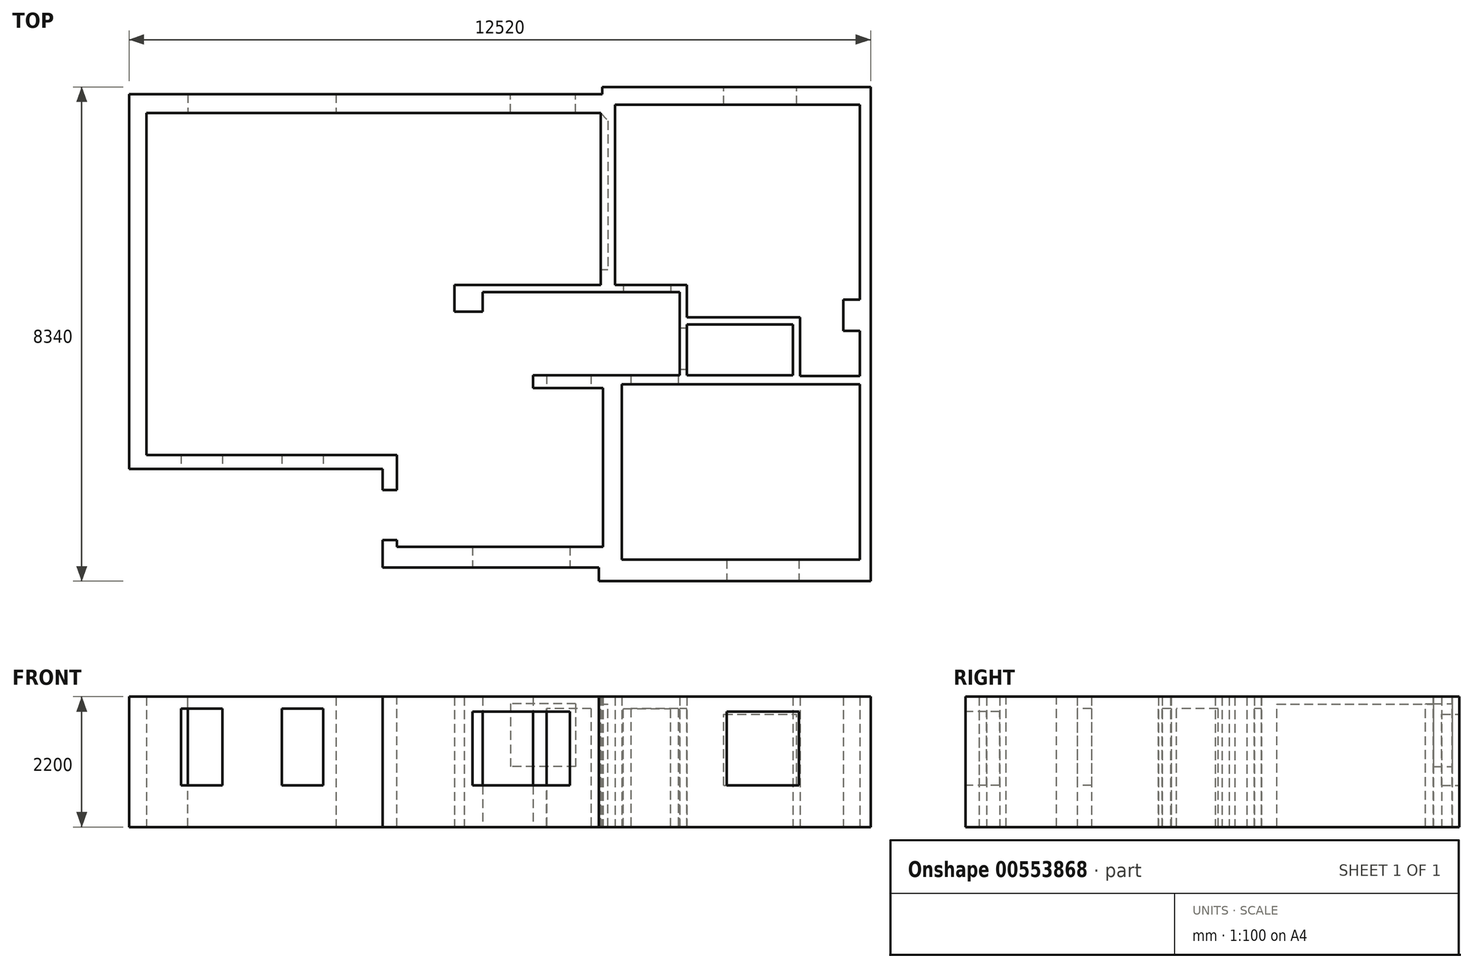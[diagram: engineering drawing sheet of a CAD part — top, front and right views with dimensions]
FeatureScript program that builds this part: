
annotation { "Feature Type Name" : "Feature", "Feature Type Description" : "" }
export const myFeature = defineFeature(function(context is Context, id is Id, definition is map)
    precondition{}
    {
        {
            var Q0;
            Q0=qCreatedBy(makeId("Top.planeOp"),FACE);
            var sketch = newSketch(context, id + "F0", { "sketchPlane" : qUnion([Q0])});
            skLineSegment(sketch, "E0", {"start": v(890, -1585.96) * mm, "end": v(-3390, -1585.96) * mm});
            skLineSegment(sketch, "E1", {"start": v(-3390, 4744.04) * mm, "end": v(-3390, -1585.96) * mm});
            skLineSegment(sketch, "E2", {"start": v(890, -3245.96) * mm, "end": v(4540, -3245.96) * mm});
            skLineSegment(sketch, "E3", {"start": v(4610, -2895.96) * mm, "end": v(1130, -2895.96) * mm});
            skLineSegment(sketch, "E4", {"start": v(4540, -3245.96) * mm, "end": v(4540, -3475.96) * mm});
            skLineSegment(sketch, "E5", {"start": v(4540, -3475.96) * mm, "end": v(9130, -3475.96) * mm});
            skLineSegment(sketch, "E6", {"start": v(9130, -3475.96) * mm, "end": v(9130, 4864.04) * mm});
            skLineSegment(sketch, "E7", {"start": v(9130, 4864.04) * mm, "end": v(4600, 4864.04) * mm});
            skLineSegment(sketch, "E8", {"start": v(4815, 4564.04) * mm, "end": v(8950, 4564.04) * mm});
            skLineSegment(sketch, "E9", {"start": v(8950, -3115.96) * mm, "end": v(4930, -3115.96) * mm});
            skLineSegment(sketch, "E10", {"start": v(8950, -155.96) * mm, "end": v(4930, -155.96) * mm});
            skLineSegment(sketch, "E11.bottom", {"start": v(8950, 1274.04) * mm, "end": v(8670, 1274.04) * mm});
            skLineSegment(sketch, "E11.top", {"start": v(8950, 744.04) * mm, "end": v(8670, 744.04) * mm});
            skLineSegment(sketch, "E11.right", {"start": v(8670, 1274.04) * mm, "end": v(8670, 744.04) * mm});
            skLineSegment(sketch, "E12", {"start": v(2020, 4424.04) * mm, "end": v(2020, 1518.96) * mm});
            skLineSegment(sketch, "E13", {"start": v(2020, 1518.96) * mm, "end": v(1110, 1518.96) * mm});
            skLineSegment(sketch, "E14", {"start": v(5905, 1400) * mm, "end": v(5905, 0) * mm});
            skLineSegment(sketch, "E15", {"start": v(7935, -15.96) * mm, "end": v(7935, 974.04) * mm});
            skLineSegment(sketch, "E16", {"start": v(7935, 974.04) * mm, "end": v(6025, 974.04) * mm});
            skLineSegment(sketch, "E17", {"start": v(6025, 974.04) * mm, "end": v(6025, 1524.04) * mm});
            skLineSegment(sketch, "E18", {"start": v(6025, 1524.04) * mm, "end": v(4815, 1524.04) * mm});
            skLineSegment(sketch, "E19", {"start": v(4815, 1524.04) * mm, "end": v(4815, 4564.04) * mm});
            skLineSegment(sketch, "E20", {"start": v(4695, 1524.04) * mm, "end": v(2215, 1524.04) * mm});
            skLineSegment(sketch, "E21", {"start": v(2215, 1524.04) * mm, "end": v(2215, 4424.04) * mm});
            skLineSegment(sketch, "E22", {"start": v(2100, 1400) * mm, "end": v(2100, 1070) * mm});
            skLineSegment(sketch, "E23", {"start": v(2100, 1070) * mm, "end": v(2580, 1070) * mm});
            skLineSegment(sketch, "E24", {"start": v(2580, 1070) * mm, "end": v(2580, 1400) * mm});
            skLineSegment(sketch, "E25", {"start": v(4695, 4424.04) * mm, "end": v(4695, 1524.04) * mm});
            skLineSegment(sketch, "E26", {"start": v(4695, 4424.04) * mm, "end": v(2215, 4424.04) * mm});
            skLineSegment(sketch, "E27", {"start": v(2020, 4424.04) * mm, "end": v(-3100, 4424.04) * mm});
            skLineSegment(sketch, "E28", {"start": v(-3100, 4424.04) * mm, "end": v(-3100, -1345.96) * mm});
            skLineSegment(sketch, "E29", {"start": v(890, -1585.96) * mm, "end": v(890, -3245.96) * mm});
            skLineSegment(sketch, "E30", {"start": v(4610, -215.96) * mm, "end": v(4610, -2895.96) * mm});
            skLineSegment(sketch, "E31", {"start": v(4930, -155.96) * mm, "end": v(4930, -3115.96) * mm});
            skLineSegment(sketch, "E32", {"start": v(8950, -155.96) * mm, "end": v(8950, -3115.96) * mm});
            skLineSegment(sketch, "E33", {"start": v(8950, -15.96) * mm, "end": v(8950, 744.04) * mm});
            skLineSegment(sketch, "E34", {"start": v(8950, 1274.04) * mm, "end": v(8950, 4564.04) * mm});
            skLineSegment(sketch, "E35", {"start": v(7935, -15.96) * mm, "end": v(8950, -15.96) * mm});
            skLineSegment(sketch, "E36", {"start": v(1110, 1400) * mm, "end": v(2100, 1400) * mm});
            skLineSegment(sketch, "E37", {"start": v(2580, 1400) * mm, "end": v(5905, 1400) * mm});
            skLineSegment(sketch, "E38", {"start": v(4610, -215.96) * mm, "end": v(3430, -215.96) * mm});
            skLineSegment(sketch, "E39", {"start": v(1130, -1345.96) * mm, "end": v(1130, -2895.96) * mm});
            skLineSegment(sketch, "E40", {"start": v(4600, 4864.04) * mm, "end": v(4600, 4744.04) * mm});
            skLineSegment(sketch, "E41", {"start": v(4600, 4744.04) * mm, "end": v(-3390, 4744.04) * mm});
            skLineSegment(sketch, "E42", {"start": v(-3100, -1345.96) * mm, "end": v(1130, -1345.96) * mm});
            skLineSegment(sketch, "E43", {"start": v(1110, 1400) * mm, "end": v(1110, 1518.96) * mm});
            skLineSegment(sketch, "E44", {"start": v(3430, -215.96) * mm, "end": v(3430, 0) * mm});
            skLineSegment(sketch, "E45", {"start": v(3430, 0) * mm, "end": v(5905, 0) * mm});
            skLineSegment(sketch, "E46.bottom", {"start": v(7815, 854.04) * mm, "end": v(6025, 854.04) * mm});
            skLineSegment(sketch, "E46.top", {"start": v(7815, 0) * mm, "end": v(6025, 0) * mm});
            skLineSegment(sketch, "E46.left", {"start": v(7815, 854.04) * mm, "end": v(7815, 0) * mm});
            skLineSegment(sketch, "E46.right", {"start": v(6025, 854.04) * mm, "end": v(6025, 0) * mm});
            skSolve(sketch);
        }
        {
            var Q0;
            Q0=makeQuery(id+"F0.imprint","IMPRINT",FACE,{"disambiguationData":[TD([[makeQuery(id+"F0.imprint","IMPRINT",EDGE,{"derivedFrom":sQuery(id+"F0.wireOp",EDGE,"E0")}),-1.0]])]});
            extrude(context, id + "F1", {"entities" : qUnion([Q0]), "depth" : 2200 * mm});
        }
        {
            var Q0;
            Q0=makeQuery(id+"F1.opExtrude","SWEPT_FACE",FACE,{"disambiguationData":[OSD([sQuery(id+"F0.wireOp",EDGE,"E27")])]});
            var sketch = newSketch(context, id + "F2", { "sketchPlane" : qUnion([Q0])});
            skLineSegment(sketch, "E47", {"start": v(-2400, 0) * mm, "end": v(-2400, 2199) * mm});
            skLineSegment(sketch, "E48", {"start": v(-2400, 2199) * mm, "end": v(100, 2199) * mm});
            skLineSegment(sketch, "E49", {"start": v(100, 2199) * mm, "end": v(100, 0) * mm});
            skLineSegment(sketch, "E50", {"start": v(100, 0) * mm, "end": v(-2400, 0) * mm});
            skSolve(sketch);
        }
        {
            var Q0;
            Q0=qSketchRegion(id+"F2",true);
            extrude(context, id + "F3", {"entities" : qUnion([Q0]), "operationType" : NewBodyOperationType.REMOVE, "oppositeDirection" : true, "depth" : 350 * mm});
        }
        {
            var Q0;
            Q0=makeQuery(id+"F1.opExtrude","SWEPT_FACE",FACE,{"disambiguationData":[OSD([sQuery(id+"F0.wireOp",EDGE,"E12")])]});
            var sketch = newSketch(context, id + "F4", { "sketchPlane" : qUnion([Q0])});
            skLineSegment(sketch, "E51", {"start": v(-4424.04, 0) * mm, "end": v(-4424.04, 2200) * mm});
            skLineSegment(sketch, "E52", {"start": v(-4424.04, 2200) * mm, "end": v(-1518.96, 2200) * mm});
            skLineSegment(sketch, "E53", {"start": v(-1518.96, 2200) * mm, "end": v(-1518.96, 0) * mm});
            skLineSegment(sketch, "E54", {"start": v(-1518.96, 0) * mm, "end": v(-4424.04, 0) * mm});
            skSolve(sketch);
        }
        {
            var Q0;
            Q0=qSketchRegion(id+"F4",true);
            extrude(context, id + "F5", {"entities" : qUnion([Q0]), "operationType" : NewBodyOperationType.REMOVE, "oppositeDirection" : true, "depth" : 250 * mm});
        }
        {
            var Q0;
            Q0=makeQuery(id+"F1.opExtrude","SWEPT_FACE",FACE,{"disambiguationData":[OSD([sQuery(id+"F0.wireOp",EDGE,"E36")])]});
            var sketch = newSketch(context, id + "F6", { "sketchPlane" : qUnion([Q0])});
            skLineSegment(sketch, "E55.bottom", {"start": v(1110, 0) * mm, "end": v(2100, 0) * mm});
            skLineSegment(sketch, "E55.top", {"start": v(1110, 2200) * mm, "end": v(2100, 2200) * mm});
            skLineSegment(sketch, "E55.left", {"start": v(1110, 0) * mm, "end": v(1110, 2200) * mm});
            skLineSegment(sketch, "E55.right", {"start": v(2100, 0) * mm, "end": v(2100, 2200) * mm});
            skSolve(sketch);
        }
        {
            var Q0;
            Q0=qSketchRegion(id+"F6",true);
            extrude(context, id + "F7", {"entities" : qUnion([Q0]), "operationType" : NewBodyOperationType.REMOVE, "oppositeDirection" : true, "depth" : 130 * mm});
        }
        {
            var Q0;
            Q0=makeQuery(id+"F1.opExtrude","SWEPT_FACE",FACE,{"disambiguationData":[OSD([sQuery(id+"F0.wireOp",EDGE,"E38")])]});
            var sketch = newSketch(context, id + "F8", { "sketchPlane" : qUnion([Q0])});
            skLineSegment(sketch, "E56.bottom", {"start": v(3660, 0) * mm, "end": v(4410, 0) * mm});
            skLineSegment(sketch, "E56.top", {"start": v(3660, 2000) * mm, "end": v(4410, 2000) * mm});
            skLineSegment(sketch, "E56.left", {"start": v(3660, 0) * mm, "end": v(3660, 2000) * mm});
            skLineSegment(sketch, "E56.right", {"start": v(4410, 0) * mm, "end": v(4410, 2000) * mm});
            skSolve(sketch);
        }
        {
            var Q0;
            Q0=qSketchRegion(id+"F8",true);
            extrude(context, id + "F9", {"entities" : qUnion([Q0]), "operationType" : NewBodyOperationType.REMOVE, "oppositeDirection" : true, "depth" : 250 * mm});
        }
        {
            var Q0;
            Q0=makeQuery(id+"F1.opExtrude","SWEPT_FACE",FACE,{"disambiguationData":[OSD([sQuery(id+"F0.wireOp",EDGE,"E37")])]});
            var sketch = newSketch(context, id + "F10", { "sketchPlane" : qUnion([Q0])});
            skLineSegment(sketch, "E57.bottom", {"start": v(4955, 0) * mm, "end": v(5755, 0) * mm});
            skLineSegment(sketch, "E57.top", {"start": v(4955, 2000) * mm, "end": v(5755, 2000) * mm});
            skLineSegment(sketch, "E57.left", {"start": v(4955, 0) * mm, "end": v(4955, 2000) * mm});
            skLineSegment(sketch, "E57.right", {"start": v(5755, 0) * mm, "end": v(5755, 2000) * mm});
            skSolve(sketch);
        }
        {
            var Q0;
            Q0=qSketchRegion(id+"F10",true);
            extrude(context, id + "F11", {"entities" : qUnion([Q0]), "operationType" : NewBodyOperationType.REMOVE, "oppositeDirection" : true, "depth" : 200 * mm});
        }
        {
            var Q0;
            Q0=makeQuery(id+"F1.opExtrude","SWEPT_FACE",FACE,{"disambiguationData":[OSD([sQuery(id+"F0.wireOp",EDGE,"E10")])]});
            var sketch = newSketch(context, id + "F12", { "sketchPlane" : qUnion([Q0])});
            skLineSegment(sketch, "E58.bottom", {"start": v(5080, 0) * mm, "end": v(5880, 0) * mm});
            skLineSegment(sketch, "E58.top", {"start": v(5080, 2000) * mm, "end": v(5880, 2000) * mm});
            skLineSegment(sketch, "E58.left", {"start": v(5080, 0) * mm, "end": v(5080, 2000) * mm});
            skLineSegment(sketch, "E58.right", {"start": v(5880, 0) * mm, "end": v(5880, 2000) * mm});
            skSolve(sketch);
        }
        {
            var Q0;
            Q0=qSketchRegion(id+"F12",true);
            extrude(context, id + "F13", {"entities" : qUnion([Q0]), "operationType" : NewBodyOperationType.REMOVE, "oppositeDirection" : true, "depth" : 200 * mm});
        }
        {
            var Q0;
            Q0=makeQuery(id+"F1.opExtrude","SWEPT_FACE",FACE,{"disambiguationData":[OSD([sQuery(id+"F0.wireOp",EDGE,"E0")])]});
            var sketch = newSketch(context, id + "F14", { "sketchPlane" : qUnion([Q0])});
            skLineSegment(sketch, "E59.bottom", {"start": v(-2515, 2000) * mm, "end": v(-1815, 2000) * mm});
            skLineSegment(sketch, "E59.top", {"start": v(-2515, 700) * mm, "end": v(-1815, 700) * mm});
            skLineSegment(sketch, "E59.left", {"start": v(-2515, 2000) * mm, "end": v(-2515, 700) * mm});
            skLineSegment(sketch, "E59.right", {"start": v(-1815, 2000) * mm, "end": v(-1815, 700) * mm});
            skLineSegment(sketch, "E60.bottom", {"start": v(-815, 2000) * mm, "end": v(-115, 2000) * mm});
            skLineSegment(sketch, "E60.top", {"start": v(-815, 700) * mm, "end": v(-115, 700) * mm});
            skLineSegment(sketch, "E60.left", {"start": v(-815, 2000) * mm, "end": v(-815, 700) * mm});
            skLineSegment(sketch, "E60.right", {"start": v(-115, 2000) * mm, "end": v(-115, 700) * mm});
            skSolve(sketch);
        }
        {
            var Q0;
            Q0=qSketchRegion(id+"F14",true);
            extrude(context, id + "F15", {"entities" : qUnion([Q0]), "operationType" : NewBodyOperationType.REMOVE, "endBound" : BoundingType.UP_TO_NEXT, "oppositeDirection" : true, "depth" : 350 * mm});
        }
        {
            var Q0;
            Q0=makeQuery(id+"F1.opExtrude","SWEPT_FACE",FACE,{"disambiguationData":[OSD([sQuery(id+"F0.wireOp",EDGE,"E2")])]});
            var sketch = newSketch(context, id + "F16", { "sketchPlane" : qUnion([Q0])});
            skLineSegment(sketch, "E61.bottom", {"start": v(2410, 1950) * mm, "end": v(4050, 1950) * mm});
            skLineSegment(sketch, "E61.top", {"start": v(2410, 700) * mm, "end": v(4050, 700) * mm});
            skLineSegment(sketch, "E61.left", {"start": v(2410, 1950) * mm, "end": v(2410, 700) * mm});
            skLineSegment(sketch, "E61.right", {"start": v(4050, 1950) * mm, "end": v(4050, 700) * mm});
            skSolve(sketch);
        }
        {
            var Q0;
            Q0=qSketchRegion(id+"F16",true);
            extrude(context, id + "F17", {"entities" : qUnion([Q0]), "operationType" : NewBodyOperationType.REMOVE, "endBound" : BoundingType.UP_TO_NEXT, "oppositeDirection" : true, "depth" : 25 * mm});
        }
        {
            var Q0;
            Q0=makeQuery(id+"F1.opExtrude","SWEPT_FACE",FACE,{"disambiguationData":[OSD([sQuery(id+"F0.wireOp",EDGE,"E5")])]});
            var sketch = newSketch(context, id + "F18", { "sketchPlane" : qUnion([Q0])});
            skLineSegment(sketch, "E62.bottom", {"start": v(6700, 1950) * mm, "end": v(7920, 1950) * mm});
            skLineSegment(sketch, "E62.top", {"start": v(6700, 700) * mm, "end": v(7920, 700) * mm});
            skLineSegment(sketch, "E62.left", {"start": v(6700, 1950) * mm, "end": v(6700, 700) * mm});
            skLineSegment(sketch, "E62.right", {"start": v(7920, 1950) * mm, "end": v(7920, 700) * mm});
            skSolve(sketch);
        }
        {
            var Q0;
            Q0=qSketchRegion(id+"F18",true);
            extrude(context, id + "F19", {"entities" : qUnion([Q0]), "operationType" : NewBodyOperationType.REMOVE, "endBound" : BoundingType.UP_TO_NEXT, "oppositeDirection" : true, "depth" : 25 * mm});
        }
        {
            var Q0;
            Q0=makeQuery(id+"F1.opExtrude","SWEPT_FACE",FACE,{"disambiguationData":[OSD([sQuery(id+"F0.wireOp",EDGE,"E7")])]});
            var sketch = newSketch(context, id + "F20", { "sketchPlane" : qUnion([Q0])});
            skLineSegment(sketch, "E63.bottom", {"start": v(-7880, 1900) * mm, "end": v(-6650, 1900) * mm});
            skLineSegment(sketch, "E63.top", {"start": v(-7880, 700) * mm, "end": v(-6650, 700) * mm});
            skLineSegment(sketch, "E63.left", {"start": v(-7880, 1900) * mm, "end": v(-7880, 700) * mm});
            skLineSegment(sketch, "E63.right", {"start": v(-6650, 1900) * mm, "end": v(-6650, 700) * mm});
            skSolve(sketch);
        }
        {
            var Q0;
            Q0=qSketchRegion(id+"F20",true);
            extrude(context, id + "F21", {"entities" : qUnion([Q0]), "operationType" : NewBodyOperationType.REMOVE, "endBound" : BoundingType.UP_TO_NEXT, "oppositeDirection" : true, "depth" : 25 * mm});
        }
        {
            var Q0;
            Q0=makeQuery(id+"F1.opExtrude","SWEPT_FACE",FACE,{"disambiguationData":[OSD([sQuery(id+"F0.wireOp",EDGE,"E41")])]});
            var sketch = newSketch(context, id + "F22", { "sketchPlane" : qUnion([Q0])});
            skLineSegment(sketch, "E64.bottom", {"start": v(-4150, 2080) * mm, "end": v(-3050, 2080) * mm});
            skLineSegment(sketch, "E64.top", {"start": v(-4150, 1020) * mm, "end": v(-3050, 1020) * mm});
            skLineSegment(sketch, "E64.left", {"start": v(-4150, 2080) * mm, "end": v(-4150, 1020) * mm});
            skLineSegment(sketch, "E64.right", {"start": v(-3050, 2080) * mm, "end": v(-3050, 1020) * mm});
            skSolve(sketch);
        }
        {
            var Q0;
            Q0=qSketchRegion(id+"F22",true);
            extrude(context, id + "F23", {"entities" : qUnion([Q0]), "operationType" : NewBodyOperationType.REMOVE, "endBound" : BoundingType.UP_TO_NEXT, "oppositeDirection" : true, "depth" : 25 * mm});
        }
        {
            var Q0;
            Q0=makeQuery(id+"F1.opExtrude","SWEPT_FACE",FACE,{"disambiguationData":[OSD([sQuery(id+"F0.wireOp",EDGE,"E29")])]});
            var sketch = newSketch(context, id + "F24", { "sketchPlane" : qUnion([Q0])});
            skLineSegment(sketch, "E65.bottom", {"start": v(1935.96, 0) * mm, "end": v(2785.96, 0) * mm});
            skLineSegment(sketch, "E65.top", {"start": v(1935.96, 2200) * mm, "end": v(2785.96, 2200) * mm});
            skLineSegment(sketch, "E65.left", {"start": v(1935.96, 0) * mm, "end": v(1935.96, 2200) * mm});
            skLineSegment(sketch, "E65.right", {"start": v(2785.96, 0) * mm, "end": v(2785.96, 2200) * mm});
            skSolve(sketch);
        }
        {
            var Q0;
            Q0=qSketchRegion(id+"F24",true);
            extrude(context, id + "F25", {"entities" : qUnion([Q0]), "operationType" : NewBodyOperationType.REMOVE, "endBound" : BoundingType.UP_TO_NEXT, "oppositeDirection" : true, "depth" : 25 * mm});
        }
        {
            var Q0;
            Q0=makeQuery(id+"F1.opExtrude","SWEPT_FACE",FACE,{"disambiguationData":[OSD([sQuery(id+"F0.wireOp",EDGE,"E14")])]});
            var sketch = newSketch(context, id + "F26", { "sketchPlane" : qUnion([Q0])});
            skLineSegment(sketch, "E66.bottom", {"start": v(-790, 0) * mm, "end": v(-90, 0) * mm});
            skLineSegment(sketch, "E66.top", {"start": v(-790, 2000) * mm, "end": v(-90, 2000) * mm});
            skLineSegment(sketch, "E66.left", {"start": v(-790, 0) * mm, "end": v(-790, 2000) * mm});
            skLineSegment(sketch, "E66.right", {"start": v(-90, 0) * mm, "end": v(-90, 2000) * mm});
            skSolve(sketch);
        }
        {
            var Q0;
            Q0=qSketchRegion(id+"F26",true);
            extrude(context, id + "F27", {"entities" : qUnion([Q0]), "operationType" : NewBodyOperationType.REMOVE, "endBound" : BoundingType.UP_TO_NEXT, "oppositeDirection" : true, "depth" : 25 * mm});
        }
        {
            var Q0;
            Q0=makeQuery(id+"F1.opExtrude","SWEPT_FACE",FACE,{"disambiguationData":[OSD([sQuery(id+"F0.wireOp",EDGE,"E25")])]});
            var sketch = newSketch(context, id + "F28", { "sketchPlane" : qUnion([Q0])});
            skLineSegment(sketch, "E67", {"start": v(-1784.04, 0) * mm, "end": v(-1784.04, 2075) * mm});
            skLineSegment(sketch, "E68", {"start": v(-1784.04, 2075) * mm, "end": v(-4424.04, 2075) * mm});
            skLineSegment(sketch, "E69", {"start": v(-4424.04, 2075) * mm, "end": v(-4424.04, 2200) * mm});
            skLineSegment(sketch, "E70", {"start": v(-4424.04, 2200) * mm, "end": v(-1524.04, 2200) * mm});
            skLineSegment(sketch, "E71", {"start": v(-1524.04, 2200) * mm, "end": v(-1524.04, 0) * mm});
            skLineSegment(sketch, "E72", {"start": v(-1524.04, 0) * mm, "end": v(-1784.04, 0) * mm});
            skSolve(sketch);
        }
        {
            var Q0;
            Q0=makeQuery(id+"F28.imprint","IMPRINT",FACE,{"disambiguationData":[TD([[makeQuery(id+"F28.imprint","IMPRINT",EDGE,{"derivedFrom":sQuery(id+"F28.wireOp",EDGE,"E67")}),-1.0]])]});
            extrude(context, id + "F29", {"entities" : qUnion([Q0]), "operationType" : NewBodyOperationType.ADD, "depth" : 125 * mm, "offsetDistance" : 25 * mm});
        }
        {
            var Q0;
            Q0=makeQuery(id+"F29.opExtrude","SWEPT_FACE",FACE,{"disambiguationData":[OSD([sQuery(id+"F28.wireOp",EDGE,"E68")])]});
            var sketch = newSketch(context, id + "F30", { "sketchPlane" : qUnion([Q0])});
            skLineSegment(sketch, "E73", {"start": v(4570, -4424.04) * mm, "end": v(4695, -4288.74) * mm});
            skLineSegment(sketch, "E74", {"start": v(4695, -4288.74) * mm, "end": v(4695, -4424.04) * mm});
            skLineSegment(sketch, "E75", {"start": v(4695, -4424.04) * mm, "end": v(4570, -4424.04) * mm});
            skSolve(sketch);
        }
        {
            var Q0;
            Q0=makeQuery(id+"F30.imprint","IMPRINT",FACE,{"disambiguationData":[TD([[makeQuery(id+"F30.imprint","IMPRINT",EDGE,{"derivedFrom":sQuery(id+"F30.wireOp",EDGE,"E73")}),-1.0]])]});
            extrude(context, id + "F31", {"entities" : qUnion([Q0]), "operationType" : NewBodyOperationType.ADD, "depth" : 2075 * mm, "offsetDistance" : 25 * mm});
        }
    });
